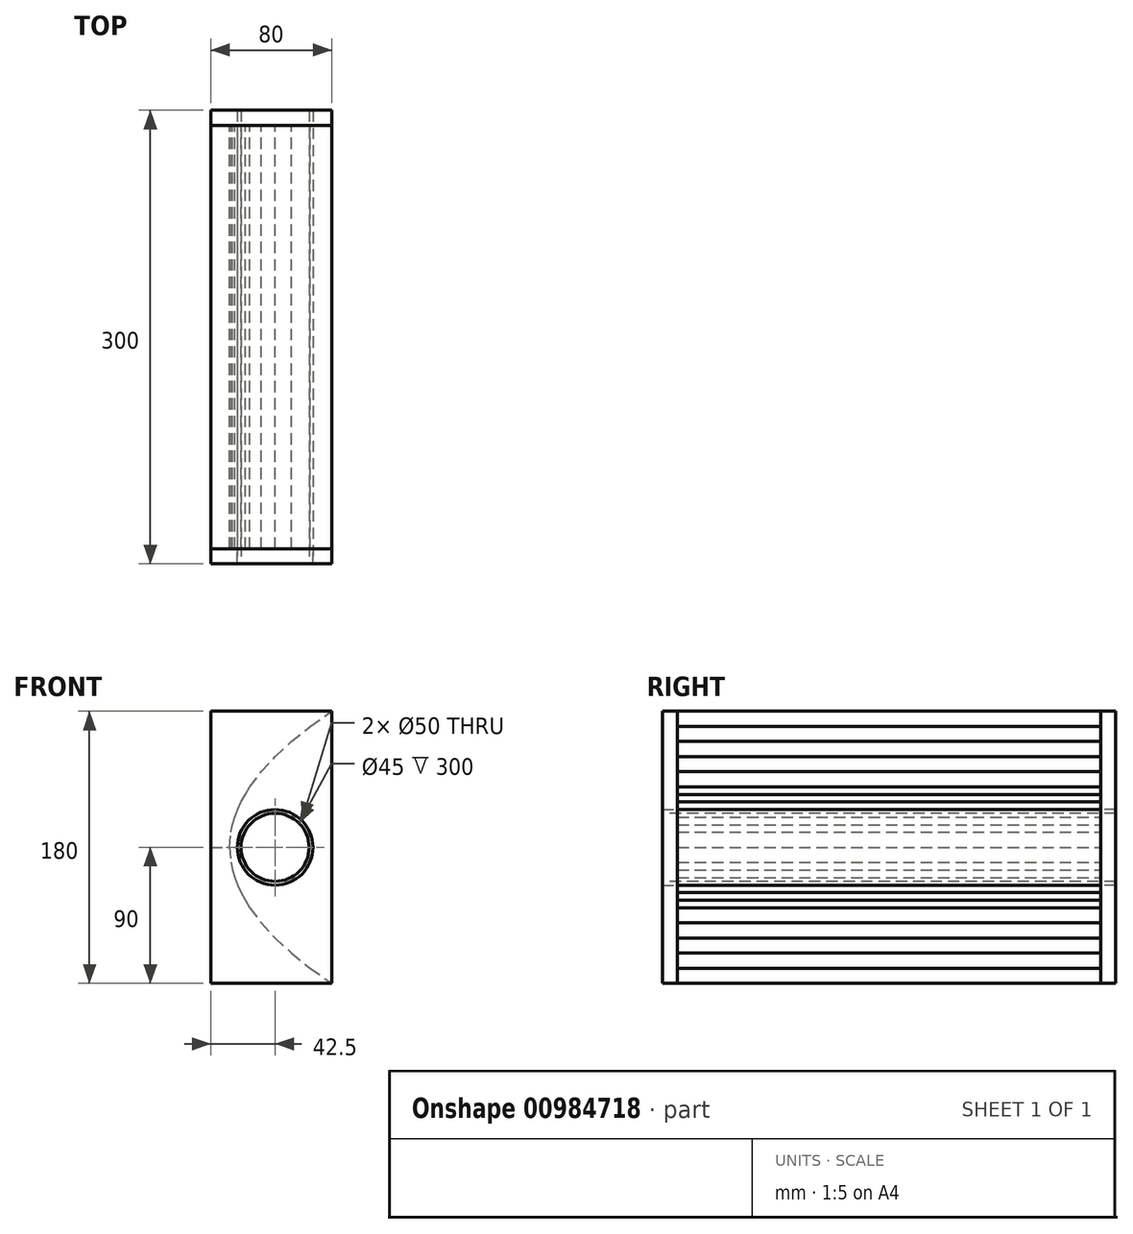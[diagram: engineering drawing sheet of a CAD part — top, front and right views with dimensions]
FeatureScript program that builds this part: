
annotation { "Feature Type Name" : "Feature", "Feature Type Description" : "" }
export const myFeature = defineFeature(function(context is Context, id is Id, definition is map)
    precondition{}
    {
        {
            var Q0;
            Q0=qCreatedBy(makeId("Front.planeOp"),FACE);
            var sketch = newSketch(context, id + "F0", { "sketchPlane" : qUnion([Q0])});
            skCircle(sketch, "E0", {"center": v(30, 0) * mm, "radius": 25 * mm});
            skCircle(sketch, "E1", {"center": v(30, 0) * mm, "radius": 22.5 * mm});
            skSolve(sketch);
        }
        {
            var Q0;
            Q0=makeQuery(id+"F0.imprint","IMPRINT",FACE,{"disambiguationData":[TD([[makeQuery(id+"F0.imprint","IMPRINT",EDGE,{"derivedFrom":sQuery(id+"F0.wireOp",EDGE,"E0")}),1.0]])]});
            extrude(context, id + "F1", {"entities" : qUnion([Q0]), "endBound" : BoundingType.SYMMETRIC, "oppositeDirection" : true, "depth" : 300 * mm, "offsetDistance" : 25 * mm});
        }
        {
            var Q0;
            Q0=qCreatedBy(makeId("Front.planeOp"),FACE);
            var sketch = newSketch(context, id + "F2", { "sketchPlane" : qUnion([Q0])});
            skCircle(sketch, "E2.0", {"center": v(30, 0) * mm, "radius": 22.5 * mm});
            skLineSegment(sketch, "E3", {"start": v(0, 0) * mm, "end": v(0.83, 10) * mm});
            skLineSegment(sketch, "E4", {"start": v(0.83, 10) * mm, "end": v(1.87, 15) * mm});
            skLineSegment(sketch, "E5", {"start": v(1.87, 15) * mm, "end": v(3.33, 20) * mm});
            skLineSegment(sketch, "E6", {"start": v(3.33, 20) * mm, "end": v(5.2, 25) * mm});
            skLineSegment(sketch, "E7", {"start": v(5.2, 25) * mm, "end": v(7.5, 30) * mm});
            skLineSegment(sketch, "E8", {"start": v(7.5, 30) * mm, "end": v(10.2, 35) * mm});
            skLineSegment(sketch, "E9", {"start": v(10.2, 35) * mm, "end": v(13.33, 40) * mm});
            skLineSegment(sketch, "E10", {"start": v(13.33, 40) * mm, "end": v(20.83, 50) * mm});
            skLineSegment(sketch, "E11", {"start": v(20.83, 50) * mm, "end": v(30, 60) * mm});
            skLineSegment(sketch, "E12", {"start": v(30, 60) * mm, "end": v(40.83, 70) * mm});
            skLineSegment(sketch, "E13", {"start": v(40.83, 70) * mm, "end": v(53.33, 80) * mm});
            skLineSegment(sketch, "E14", {"start": v(53.33, 80) * mm, "end": v(67.5, 90) * mm});
            skLineSegment(sketch, "E15", {"start": v(67.5, 90) * mm, "end": v(-12.5, 90) * mm});
            skLineSegment(sketch, "E16", {"start": v(-12.5, 90) * mm, "end": v(-12.5, 0) * mm});
            skLineSegment(sketch, "E17", {"start": v(-12.5, 0) * mm, "end": v(0, 0) * mm});
            skSolve(sketch);
        }
        {
            var Q0;
            Q0=makeQuery(id+"F2.imprint","IMPRINT",FACE,{"disambiguationData":[TD([[makeQuery(id+"F2.imprint","IMPRINT",EDGE,{"derivedFrom":sQuery(id+"F2.wireOp",EDGE,"E3")}),1.0]])]});
            extrude(context, id + "F3", {"entities" : qUnion([Q0]), "endBound" : BoundingType.SYMMETRIC, "depth" : 280 * mm, "offsetDistance" : 25 * mm});
        }
        {
            var Q0;
            Q0=makeQuery(id+"F3.opExtrude","SWEPT_BODY",BODY,{"disambiguationData":[OSD([sQuery(id+"F2.wireOp",EDGE,"E3"),sQuery(id+"F2.wireOp",EDGE,"E4"),sQuery(id+"F2.wireOp",EDGE,"E5"),sQuery(id+"F2.wireOp",EDGE,"E6"),sQuery(id+"F2.wireOp",EDGE,"E7"),sQuery(id+"F2.wireOp",EDGE,"E8"),sQuery(id+"F2.wireOp",EDGE,"E9"),sQuery(id+"F2.wireOp",EDGE,"E10"),sQuery(id+"F2.wireOp",EDGE,"E11"),sQuery(id+"F2.wireOp",EDGE,"E12"),sQuery(id+"F2.wireOp",EDGE,"E13"),sQuery(id+"F2.wireOp",EDGE,"E14"),sQuery(id+"F2.wireOp",EDGE,"E15"),sQuery(id+"F2.wireOp",EDGE,"E16"),sQuery(id+"F2.wireOp",EDGE,"E17")])]});
            var Q1;
            Q1=qCreatedBy(makeId("Top.planeOp"),FACE);
            mirror(context, id + "F4", {"operationType" : NewBodyOperationType.ADD, "entities" : qUnion([Q0]), "mirrorPlane" : qUnion([Q1])});
        }
        {
            var Q0;
            {var subQ0=makeQuery(id+"F3.opExtrude","CAP_FACE",FACE,{"disambiguationData":[OSD([sQuery(id+"F2.wireOp",EDGE,"E3"),sQuery(id+"F2.wireOp",EDGE,"E4"),sQuery(id+"F2.wireOp",EDGE,"E5"),sQuery(id+"F2.wireOp",EDGE,"E6"),sQuery(id+"F2.wireOp",EDGE,"E7"),sQuery(id+"F2.wireOp",EDGE,"E8"),sQuery(id+"F2.wireOp",EDGE,"E9"),sQuery(id+"F2.wireOp",EDGE,"E10"),sQuery(id+"F2.wireOp",EDGE,"E11"),sQuery(id+"F2.wireOp",EDGE,"E12"),sQuery(id+"F2.wireOp",EDGE,"E13"),sQuery(id+"F2.wireOp",EDGE,"E14"),sQuery(id+"F2.wireOp",EDGE,"E15"),sQuery(id+"F2.wireOp",EDGE,"E16"),sQuery(id+"F2.wireOp",EDGE,"E17")])],"isStart":false});Q0=makeQuery(id+"F4.boolean.opBoolean","MERGE",FACE,{"derivedFrom":[subQ0,makeQuery(id+"F4.opPattern","COPY",FACE,{"derivedFrom":subQ0,"instanceName":"1"})]});}
            var sketch = newSketch(context, id + "F5", { "sketchPlane" : qUnion([Q0])});
            skLineSegment(sketch, "E18.0", {"start": v(67.5, 90) * mm, "end": v(-12.5, 90) * mm});
            skLineSegment(sketch, "E19.0", {"start": v(-12.5, 90) * mm, "end": v(-12.5, -90) * mm});
            skLineSegment(sketch, "E20.0", {"start": v(67.5, -90) * mm, "end": v(-12.5, -90) * mm});
            skLineSegment(sketch, "E21", {"start": v(67.5, 90) * mm, "end": v(67.5, -90) * mm});
            skCircle(sketch, "E22.0", {"center": v(30, 0) * mm, "radius": 25 * mm});
            skSolve(sketch);
        }
        {
            var Q0;
            Q0=makeQuery(id+"F5.imprint","IMPRINT",FACE,{"disambiguationData":[TD([[makeQuery(id+"F5.imprint","IMPRINT",EDGE,{"derivedFrom":sQuery(id+"F5.wireOp",EDGE,"E21")}),-1.0]])]});
            var Q1;
            Q1=makeQuery(id+"F5.imprint","IMPRINT",FACE,{"disambiguationData":[TD([[makeQuery(id+"F5.imprint","IMPRINT",EDGE,{"derivedFrom":sQuery(id+"F5.wireOp",EDGE,"E18.0")}),1.0]])]});
            extrude(context, id + "F6", {"entities" : qUnion([Q0, Q1]), "depth" : 10 * mm, "offsetDistance" : 25 * mm});
        }
        {
            var Q0;
            Q0=makeQuery(id+"F6.opExtrude","SWEPT_BODY",BODY,{"disambiguationData":[OSD([sQuery(id+"F5.wireOp",EDGE,"E18.0"),sQuery(id+"F5.wireOp",EDGE,"E19.0"),sQuery(id+"F5.wireOp",EDGE,"E20.0"),sQuery(id+"F5.wireOp",EDGE,"E21"),sQuery(id+"F5.wireOp",EDGE,"E22.0")])]});
            var Q1;
            Q1=qCreatedBy(makeId("Front.planeOp"),FACE);
            mirror(context, id + "F7", {"entities" : qUnion([Q0]), "mirrorPlane" : qUnion([Q1])});
        }
    });
